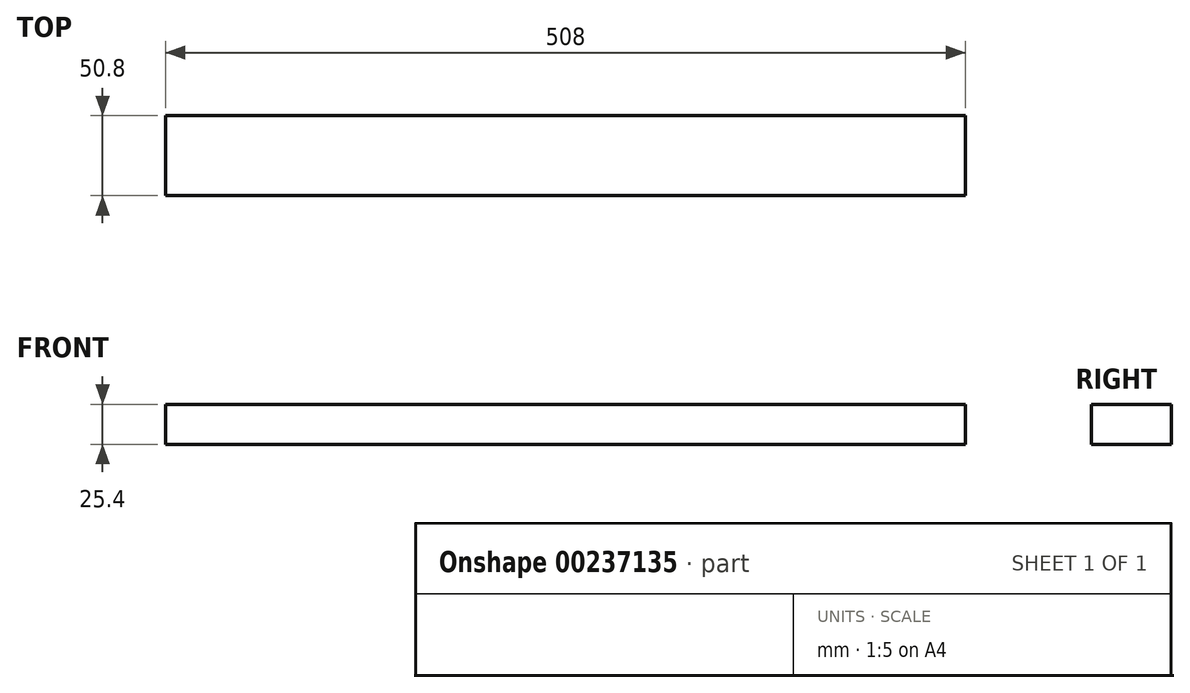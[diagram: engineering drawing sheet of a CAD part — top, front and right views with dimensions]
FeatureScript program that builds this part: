
annotation { "Feature Type Name" : "Feature", "Feature Type Description" : "" }
export const myFeature = defineFeature(function(context is Context, id is Id, definition is map)
    precondition{}
    {
        {
            var Q0;
            Q0=qCreatedBy(makeId("Top.planeOp"),FACE);
            var sketch = newSketch(context, id + "F0", { "sketchPlane" : qUnion([Q0])});
            skLineSegment(sketch, "E0.bottom", {"start": v(0, 0) * mm, "end": v(508, 0) * mm});
            skLineSegment(sketch, "E0.top", {"start": v(0, 50.8) * mm, "end": v(508, 50.8) * mm});
            skLineSegment(sketch, "E0.left", {"start": v(0, 0) * mm, "end": v(0, 50.8) * mm});
            skLineSegment(sketch, "E0.right", {"start": v(508, 0) * mm, "end": v(508, 50.8) * mm});
            skSolve(sketch);
        }
        {
            var Q0;
            Q0 = qSketchRegion(id + "F0", true);
            extrude(context, id + "F1", {"entities" : qUnion([Q0]), "depth" : 25.4 * mm});
        }
    });
